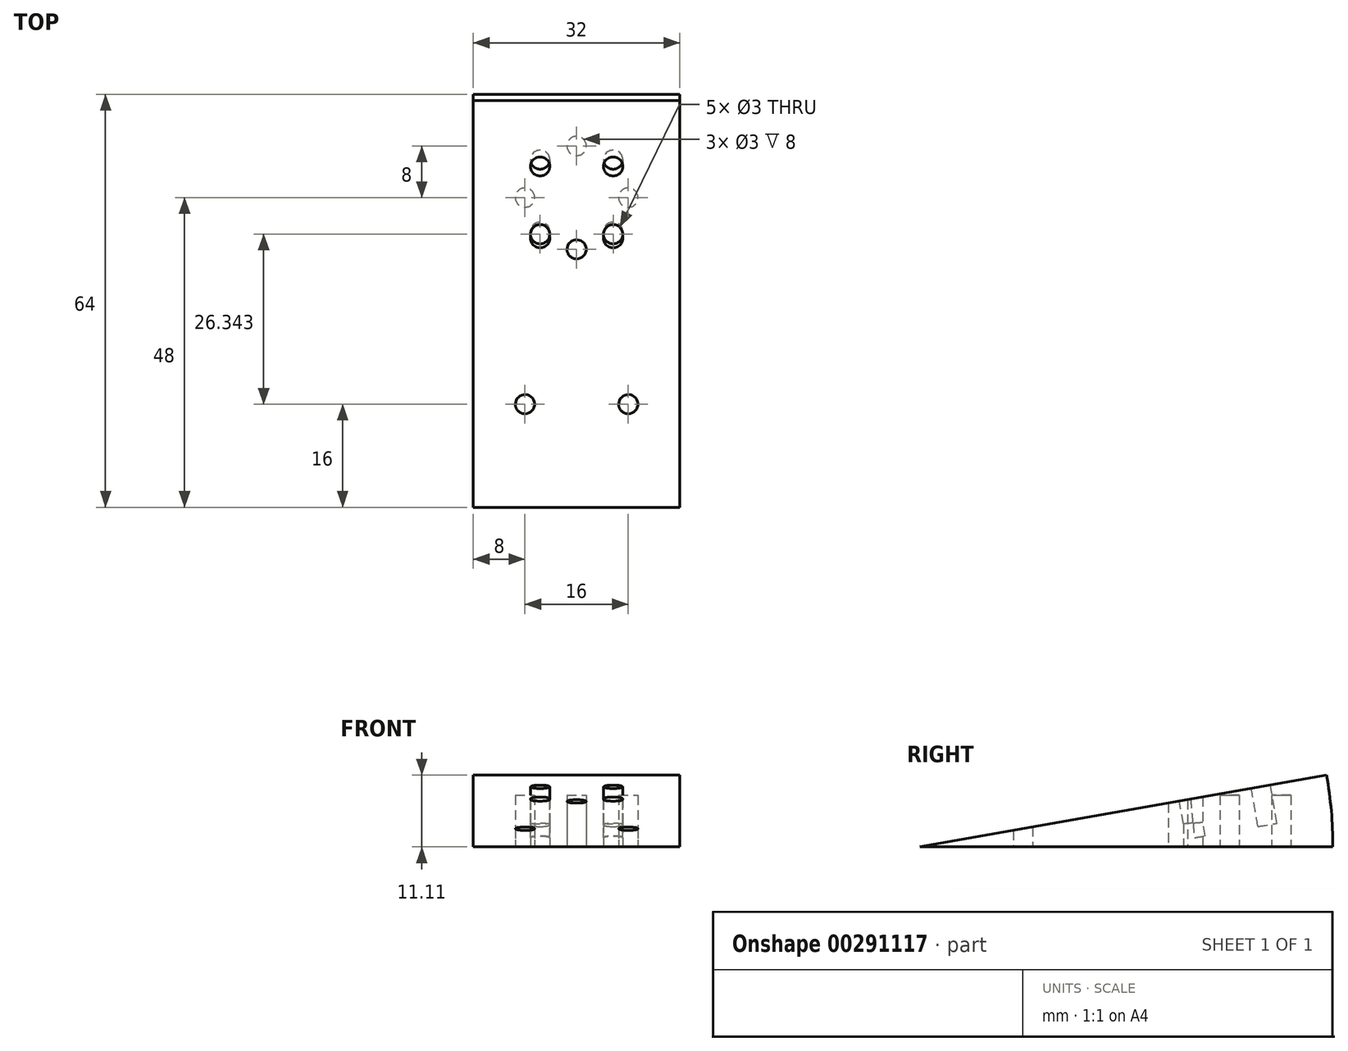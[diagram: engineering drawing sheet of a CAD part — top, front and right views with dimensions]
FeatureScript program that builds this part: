
annotation { "Feature Type Name" : "Feature", "Feature Type Description" : "" }
export const myFeature = defineFeature(function(context is Context, id is Id, definition is map)
    precondition{}
    {
        {
            var Q0;
            Q0=qCreatedBy(makeId("Top.planeOp"),FACE);
            var sketch = newSketch(context, id + "F0", { "sketchPlane" : qUnion([Q0])});
            skLineSegment(sketch, "E0.bottom", {"start": v(-16, 32) * mm, "end": v(16, 32) * mm});
            skLineSegment(sketch, "E0.top", {"start": v(-16, -32) * mm, "end": v(16, -32) * mm});
            skLineSegment(sketch, "E0.left", {"start": v(-16, 32) * mm, "end": v(-16, -32) * mm});
            skLineSegment(sketch, "E0.right", {"start": v(16, 32) * mm, "end": v(16, -32) * mm});
            skPoint(sketch, "E0.middle", {"position": v(0, 0) * mm});
            skSolve(sketch);
        }
        {
            var Q0;
            Q0=makeQuery(id+"F0.imprint","IMPRINT",FACE,{"disambiguationData":[TD([[makeQuery(id+"F0.imprint","IMPRINT",EDGE,{"derivedFrom":sQuery(id+"F0.wireOp",EDGE,"E0.bottom")}),-1.0]])]});
            var Q1;
            Q1=sQuery(id+"F0.wireOp",EDGE,"E0.top");
            revolve(context, id + "F1", {"entities" : qUnion([Q0]), "axis" : qUnion([Q1]), "revolveType" : RevolveType.ONE_DIRECTION, "angle" : 10 * degree});
        }
        {
            var Q0;
            Q0=makeQuery(id+"F1.opRevolve","CAP_FACE",FACE,{"disambiguationData":[OSD([sQuery(id+"F0.wireOp",EDGE,"E0.bottom"),sQuery(id+"F0.wireOp",EDGE,"E0.top"),sQuery(id+"F0.wireOp",EDGE,"E0.left"),sQuery(id+"F0.wireOp",EDGE,"E0.right")])],"isStart":false});
            var sketch = newSketch(context, id + "F2", { "sketchPlane" : qUnion([Q0])});
            skCircle(sketch, "E1", {"center": v(0, -23.51) * mm, "radius": 1.5 * mm});
            skCircle(sketch, "E2.1.0", {"center": v(5.66, -21.17) * mm, "radius": 1.5 * mm});
            skCircle(sketch, "E2.2.0", {"center": v(8, -15.51) * mm, "radius": 1.5 * mm});
            skCircle(sketch, "E2.3.0", {"center": v(5.66, -9.86) * mm, "radius": 1.5 * mm});
            skCircle(sketch, "E2.4.0", {"center": v(0, -7.51) * mm, "radius": 1.5 * mm});
            skCircle(sketch, "E2.5.0", {"center": v(-5.66, -9.86) * mm, "radius": 1.5 * mm});
            skCircle(sketch, "E2.6.0", {"center": v(-8, -15.51) * mm, "radius": 1.5 * mm});
            skCircle(sketch, "E2.7.0", {"center": v(-5.66, -21.17) * mm, "radius": 1.5 * mm});
            skPoint(sketch, "E2.center", {"position": v(0, -15.51) * mm});
            skCircle(sketch, "E3.0.1.0", {"center": v(0, 8.49) * mm, "radius": 1.5 * mm});
            skCircle(sketch, "E3.0.1.1", {"center": v(5.66, 10.83) * mm, "radius": 1.5 * mm});
            skCircle(sketch, "E3.0.1.2", {"center": v(8, 16.49) * mm, "radius": 1.5 * mm});
            skCircle(sketch, "E3.0.1.3", {"center": v(5.66, 22.14) * mm, "radius": 1.5 * mm});
            skCircle(sketch, "E3.0.1.4", {"center": v(0, 24.49) * mm, "radius": 1.5 * mm});
            skCircle(sketch, "E3.0.1.5", {"center": v(-5.66, 22.14) * mm, "radius": 1.5 * mm});
            skPoint(sketch, "E3.0.1.6", {"position": v(0, 16.49) * mm});
            skCircle(sketch, "E3.0.1.7", {"center": v(-5.66, 10.83) * mm, "radius": 1.5 * mm});
            skCircle(sketch, "E3.0.1.8", {"center": v(-8, 16.49) * mm, "radius": 1.5 * mm});
            skLineSegment(sketch, "E3.direction1", {"start": v(0, -23.51) * mm, "end": v(25, -23.51) * mm, "construction": true});
            skLineSegment(sketch, "E3.direction2", {"start": v(0, -23.51) * mm, "end": v(0, 8.49) * mm, "construction": true});
            skSolve(sketch);
        }
        {
            var Q0;
            Q0=makeQuery(id+"F2.imprint","IMPRINT",FACE,{"disambiguationData":[TD([[makeQuery(id+"F2.imprint","IMPRINT",EDGE,{"derivedFrom":sQuery(id+"F2.wireOp",EDGE,"E3.0.1.5")}),1.0]])]});
            var Q1;
            Q1=makeQuery(id+"F2.imprint","IMPRINT",FACE,{"disambiguationData":[TD([[makeQuery(id+"F2.imprint","IMPRINT",EDGE,{"derivedFrom":sQuery(id+"F2.wireOp",EDGE,"E3.0.1.3")}),1.0]])]});
            var Q2;
            Q2=makeQuery(id+"F2.imprint","IMPRINT",FACE,{"disambiguationData":[TD([[makeQuery(id+"F2.imprint","IMPRINT",EDGE,{"derivedFrom":sQuery(id+"F2.wireOp",EDGE,"E3.0.1.1")}),1.0]])]});
            var Q3;
            Q3=makeQuery(id+"F2.imprint","IMPRINT",FACE,{"disambiguationData":[TD([[makeQuery(id+"F2.imprint","IMPRINT",EDGE,{"derivedFrom":sQuery(id+"F2.wireOp",EDGE,"E3.0.1.7")}),1.0]])]});
            extrude(context, id + "F3", {"entities" : qUnion([Q0, Q1, Q2, Q3]), "operationType" : NewBodyOperationType.REMOVE, "oppositeDirection" : true, "depth" : 6 * mm});
        }
        {
            var Q0;
            Q0=makeQuery(id+"F1.opRevolve","CAP_FACE",FACE,{"disambiguationData":[OSD([sQuery(id+"F0.wireOp",EDGE,"E0.bottom"),sQuery(id+"F0.wireOp",EDGE,"E0.top"),sQuery(id+"F0.wireOp",EDGE,"E0.left"),sQuery(id+"F0.wireOp",EDGE,"E0.right")])],"isStart":true});
            var sketch = newSketch(context, id + "F4", { "sketchPlane" : qUnion([Q0])});
            skCircle(sketch, "E4", {"center": v(0, -8) * mm, "radius": 1.5 * mm});
            skCircle(sketch, "E5.1.0", {"center": v(-5.66, -10.34) * mm, "radius": 1.5 * mm});
            skCircle(sketch, "E5.2.0", {"center": v(-8, -16) * mm, "radius": 1.5 * mm});
            skCircle(sketch, "E5.3.0", {"center": v(-5.66, -21.66) * mm, "radius": 1.5 * mm});
            skCircle(sketch, "E5.4.0", {"center": v(0, -24) * mm, "radius": 1.5 * mm});
            skCircle(sketch, "E5.5.0", {"center": v(5.66, -21.66) * mm, "radius": 1.5 * mm});
            skCircle(sketch, "E5.6.0", {"center": v(8, -16) * mm, "radius": 1.5 * mm});
            skCircle(sketch, "E5.7.0", {"center": v(5.66, -10.34) * mm, "radius": 1.5 * mm});
            skPoint(sketch, "E5.center", {"position": v(0, -16) * mm});
            skPoint(sketch, "E6.0.1.0", {"position": v(0, 16) * mm});
            skCircle(sketch, "E6.0.1.1", {"center": v(5.66, 21.66) * mm, "radius": 1.5 * mm});
            skCircle(sketch, "E6.0.1.2", {"center": v(-5.66, 21.66) * mm, "radius": 1.5 * mm});
            skCircle(sketch, "E6.0.1.3", {"center": v(0, 24) * mm, "radius": 1.5 * mm});
            skCircle(sketch, "E6.0.1.4", {"center": v(-8, 16) * mm, "radius": 1.5 * mm});
            skCircle(sketch, "E6.0.1.5", {"center": v(-5.66, 10.34) * mm, "radius": 1.5 * mm});
            skCircle(sketch, "E6.0.1.6", {"center": v(8, 16) * mm, "radius": 1.5 * mm});
            skCircle(sketch, "E6.0.1.7", {"center": v(0, 8) * mm, "radius": 1.5 * mm});
            skCircle(sketch, "E6.0.1.8", {"center": v(5.66, 10.34) * mm, "radius": 1.5 * mm});
            skLineSegment(sketch, "E6.direction1", {"start": v(-5.66, -21.66) * mm, "end": v(19.34, -21.66) * mm, "construction": true});
            skLineSegment(sketch, "E6.direction2", {"start": v(-5.66, -21.66) * mm, "end": v(-5.66, 10.34) * mm, "construction": true});
            skSolve(sketch);
        }
        {
            var Q0;
            {var subQ0=sQuery(id+"F4.wireOp",EDGE,"E5.7.0");var subQ1=makeQuery(id+"F3.boolean.opBoolean","INTERSECT",EDGE,{"derivedFrom":[makeQuery(id+"F1.opRevolve","CAP_FACE",FACE,{"disambiguationData":[OSD([sQuery(id+"F0.wireOp",EDGE,"E0.bottom"),sQuery(id+"F0.wireOp",EDGE,"E0.top"),sQuery(id+"F0.wireOp",EDGE,"E0.left"),sQuery(id+"F0.wireOp",EDGE,"E0.right")])],"isStart":true}),makeQuery(id+"F3.opExtrude","SWEPT_FACE",FACE,{"disambiguationData":[OSD([sQuery(id+"F2.wireOp",EDGE,"E3.0.1.1")])]})]});var subQ2=makeQuery(id+"F4.imprint","INTERSECT",VERTEX,{"disambiguationData":[OD(0.0)],"derivedFrom":[subQ1,subQ0]});Q0=makeQuery(id+"F4.imprint","IMPRINT",FACE,{"disambiguationData":[TD([[makeQuery(id+"F4.imprint","IMPRINT",EDGE,{"disambiguationData":[TD([[subQ2,-1.0]])],"derivedFrom":subQ0}),1.0]])]});}
            var Q1;
            {var subQ0=sQuery(id+"F4.wireOp",EDGE,"E5.1.0");var subQ1=makeQuery(id+"F3.boolean.opBoolean","INTERSECT",EDGE,{"derivedFrom":[makeQuery(id+"F1.opRevolve","CAP_FACE",FACE,{"disambiguationData":[OSD([sQuery(id+"F0.wireOp",EDGE,"E0.bottom"),sQuery(id+"F0.wireOp",EDGE,"E0.top"),sQuery(id+"F0.wireOp",EDGE,"E0.left"),sQuery(id+"F0.wireOp",EDGE,"E0.right")])],"isStart":true}),makeQuery(id+"F3.opExtrude","SWEPT_FACE",FACE,{"disambiguationData":[OSD([sQuery(id+"F2.wireOp",EDGE,"E3.0.1.7")])]})]});var subQ2=makeQuery(id+"F4.imprint","INTERSECT",VERTEX,{"disambiguationData":[OD(0.0)],"derivedFrom":[subQ1,subQ0]});Q1=makeQuery(id+"F4.imprint","IMPRINT",FACE,{"disambiguationData":[TD([[makeQuery(id+"F4.imprint","IMPRINT",EDGE,{"disambiguationData":[TD([[subQ2,-1.0]])],"derivedFrom":subQ0}),1.0]])]});}
            var Q2;
            Q2=makeQuery(id+"F4.imprint","IMPRINT",FACE,{"disambiguationData":[TD([[makeQuery(id+"F4.imprint","IMPRINT",EDGE,{"derivedFrom":sQuery(id+"F4.wireOp",EDGE,"E4")}),1.0]])]});
            var Q3;
            Q3=makeQuery(id+"F4.imprint","IMPRINT",FACE,{"disambiguationData":[TD([[makeQuery(id+"F4.imprint","IMPRINT",EDGE,{"derivedFrom":sQuery(id+"F4.wireOp",EDGE,"E5.6.0")}),1.0]])]});
            var Q4;
            Q4=makeQuery(id+"F4.imprint","IMPRINT",FACE,{"disambiguationData":[TD([[makeQuery(id+"F4.imprint","IMPRINT",EDGE,{"derivedFrom":sQuery(id+"F4.wireOp",EDGE,"E5.4.0")}),1.0]])]});
            var Q5;
            Q5=makeQuery(id+"F4.imprint","IMPRINT",FACE,{"disambiguationData":[TD([[makeQuery(id+"F4.imprint","IMPRINT",EDGE,{"derivedFrom":sQuery(id+"F4.wireOp",EDGE,"E5.2.0")}),1.0]])]});
            var Q6;
            Q6=makeQuery(id+"F4.imprint","IMPRINT",FACE,{"disambiguationData":[TD([[makeQuery(id+"F4.imprint","IMPRINT",EDGE,{"derivedFrom":sQuery(id+"F4.wireOp",EDGE,"E6.0.1.4")}),1.0]])]});
            var Q7;
            Q7=makeQuery(id+"F4.imprint","IMPRINT",FACE,{"disambiguationData":[TD([[makeQuery(id+"F4.imprint","IMPRINT",EDGE,{"derivedFrom":sQuery(id+"F4.wireOp",EDGE,"E6.0.1.6")}),1.0]])]});
            extrude(context, id + "F5", {"entities" : qUnion([Q0, Q1, Q2, Q3, Q4, Q5, Q6, Q7]), "operationType" : NewBodyOperationType.REMOVE, "oppositeDirection" : true, "depth" : 8 * mm});
        }
    });
